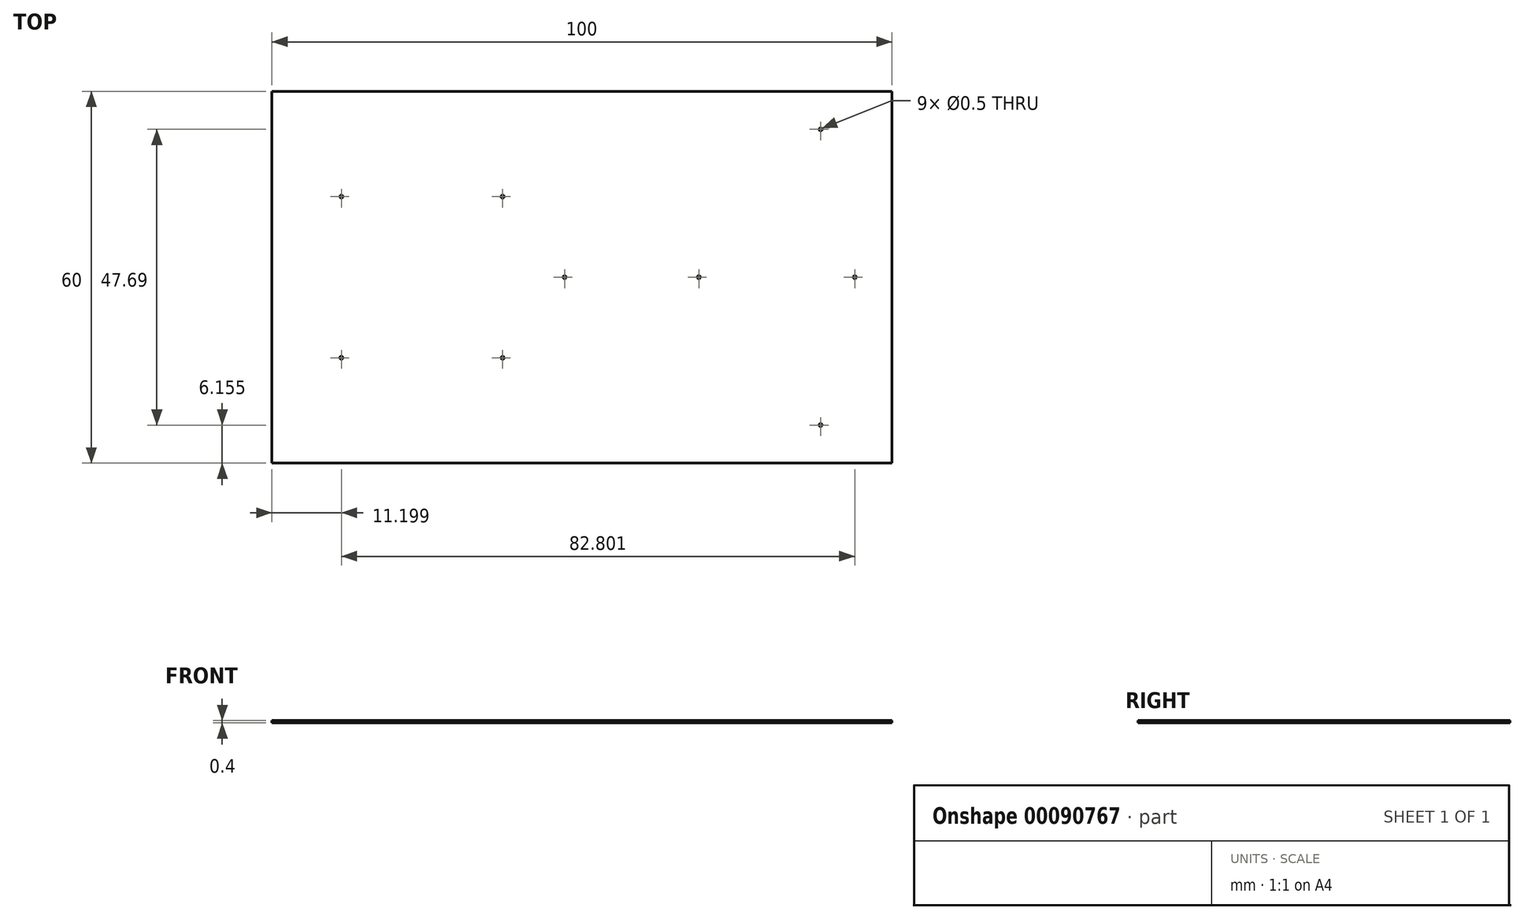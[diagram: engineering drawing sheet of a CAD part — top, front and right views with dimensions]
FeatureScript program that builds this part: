
annotation { "Feature Type Name" : "Feature", "Feature Type Description" : "" }
export const myFeature = defineFeature(function(context is Context, id is Id, definition is map)
    precondition{}
    {
        {
            var Q0;
            Q0=qCreatedBy(makeId("Top.planeOp"),FACE);
            var sketch = newSketch(context, id + "F0", { "sketchPlane" : qUnion([Q0])});
            skLineSegment(sketch, "E0.bottom", {"start": v(32.15, 30) * mm, "end": v(-67.85, 30) * mm});
            skLineSegment(sketch, "E0.top", {"start": v(32.15, -30) * mm, "end": v(-67.85, -30) * mm});
            skLineSegment(sketch, "E0.left", {"start": v(32.15, 30) * mm, "end": v(32.15, -30) * mm});
            skLineSegment(sketch, "E0.right", {"start": v(-67.85, 30) * mm, "end": v(-67.85, -30) * mm});
            skPoint(sketch, "E0.middle", {"position": v(-17.85, 0) * mm});
            skCircle(sketch, "E1.cCircle", {"center": v(6.88, 0) * mm, "radius": 13.77 * mm, "construction": true});
            skLineSegment(sketch, "E1.0", {"start": v(20.65, 23.84) * mm, "end": v(20.65, -23.84) * mm, "construction": true});
            skLineSegment(sketch, "E1.1", {"start": v(20.65, -23.84) * mm, "end": v(-20.65, 0) * mm, "construction": true});
            skLineSegment(sketch, "E1.2", {"start": v(-20.65, 0) * mm, "end": v(20.65, 23.84) * mm, "construction": true});
            skPoint(sketch, "E1.0.midPoint", {"position": v(20.65, 0) * mm});
            skLineSegment(sketch, "E2", {"start": v(-12.7, 30) * mm, "end": v(-12.7, -30) * mm, "construction": true});
            skLineSegment(sketch, "E3", {"start": v(12.7, 30) * mm, "end": v(12.7, -30) * mm, "construction": true});
            skCircle(sketch, "E4", {"center": v(-20.65, 0) * mm, "radius": 0.25 * mm});
            skCircle(sketch, "E5.1.0", {"center": v(20.65, -23.84) * mm, "radius": 0.25 * mm});
            skCircle(sketch, "E5.2.0", {"center": v(20.65, 23.84) * mm, "radius": 0.25 * mm});
            skCircle(sketch, "E6", {"center": v(26.15, 0) * mm, "radius": 0.25 * mm});
            skLineSegment(sketch, "E7.bottom", {"start": v(-30.65, 13) * mm, "end": v(-56.65, 13) * mm, "construction": true});
            skLineSegment(sketch, "E7.top", {"start": v(-30.65, -13) * mm, "end": v(-56.65, -13) * mm, "construction": true});
            skLineSegment(sketch, "E7.left", {"start": v(-30.65, 13) * mm, "end": v(-30.65, -13) * mm, "construction": true});
            skLineSegment(sketch, "E7.right", {"start": v(-56.65, 13) * mm, "end": v(-56.65, -13) * mm, "construction": true});
            skPoint(sketch, "E7.middle", {"position": v(-43.65, 0) * mm});
            skLineSegment(sketch, "E8", {"start": v(-12.7, 0) * mm, "end": v(12.7, 0) * mm, "construction": true});
            skCircle(sketch, "E9", {"center": v(-56.65, 13) * mm, "radius": 0.25 * mm});
            skCircle(sketch, "E10.1.0", {"center": v(-56.65, -13) * mm, "radius": 0.25 * mm});
            skCircle(sketch, "E10.2.0", {"center": v(-30.65, -13) * mm, "radius": 0.25 * mm});
            skCircle(sketch, "E10.3.0", {"center": v(-30.65, 13) * mm, "radius": 0.25 * mm});
            skLineSegment(sketch, "E11.0", {"start": v(-68.05, 30.2) * mm, "end": v(-68.05, -30.2) * mm});
            skLineSegment(sketch, "E11.1", {"start": v(32.35, 30.2) * mm, "end": v(-68.05, 30.2) * mm});
            skLineSegment(sketch, "E11.2", {"start": v(32.35, 30.2) * mm, "end": v(32.35, -30.2) * mm});
            skLineSegment(sketch, "E11.3", {"start": v(32.35, -30.2) * mm, "end": v(-68.05, -30.2) * mm});
            skCircle(sketch, "E12", {"center": v(1, 0) * mm, "radius": 0.25 * mm});
            skSolve(sketch);
        }
        {
            var Q0;
            Q0=makeQuery(id+"F0.imprint","IMPRINT",FACE,{"disambiguationData":[TD([[makeQuery(id+"F0.imprint","IMPRINT",EDGE,{"derivedFrom":sQuery(id+"F0.wireOp",EDGE,"E0.bottom")}),1.0]])]});
            extrude(context, id + "F1", {"entities" : qUnion([Q0]), "depth" : 0.4 * mm});
        }
    });
